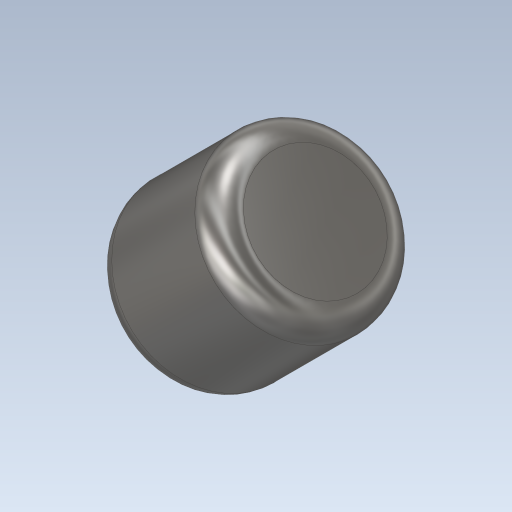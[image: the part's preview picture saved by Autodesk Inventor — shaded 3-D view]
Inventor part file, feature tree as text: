
AUTODESK INVENTOR PART (.ipt)
format: ipt  version: 2024 (Build 280153000, 153)  size: 172,544 bytes
history: native  units: mm
features: revolve x1, sketch x1
ambient origin geometry x8: Origin, YZ Plane, XZ Plane, XY Plane, X Axis, Y Axis, Z Axis, Center Point
bodies: Solid1 (feature_tree)
feature tree (2):
  revolve  "Revolution1"  [1 undecoded]
  sketch  "Sketch_1"  dims[d0=360.0deg]
note: 1 required parameter value undecoded (feature->parameter linkage not recoverable at this tier; creation-order binding heuristic only, values carry confidence <= 0.55)
